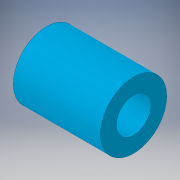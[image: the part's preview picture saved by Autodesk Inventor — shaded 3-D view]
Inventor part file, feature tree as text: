
AUTODESK INVENTOR PART (.ipt)
format: ipt  version: 2017 SP1 (Build 210196100, 196)  size: 96,256 bytes
history: native  units: in
note: dims shown in document units (in); Inventor stores cm internally (conversion verified against a paired STEP export)
features: extrude x1, sketch x1
ambient origin geometry x8: Origin, YZ Plane, XZ Plane, XY Plane, X Axis, Y Axis, Z Axis, Center Point
bodies: Solid1 (feature_tree)
feature tree (2):
  extrude  "Extrusion1"  Depth=0.657in
  sketch  "Sketch1"  dims[d0=0.26in d1=0.5in d2=0.657in d3=0.0in]
